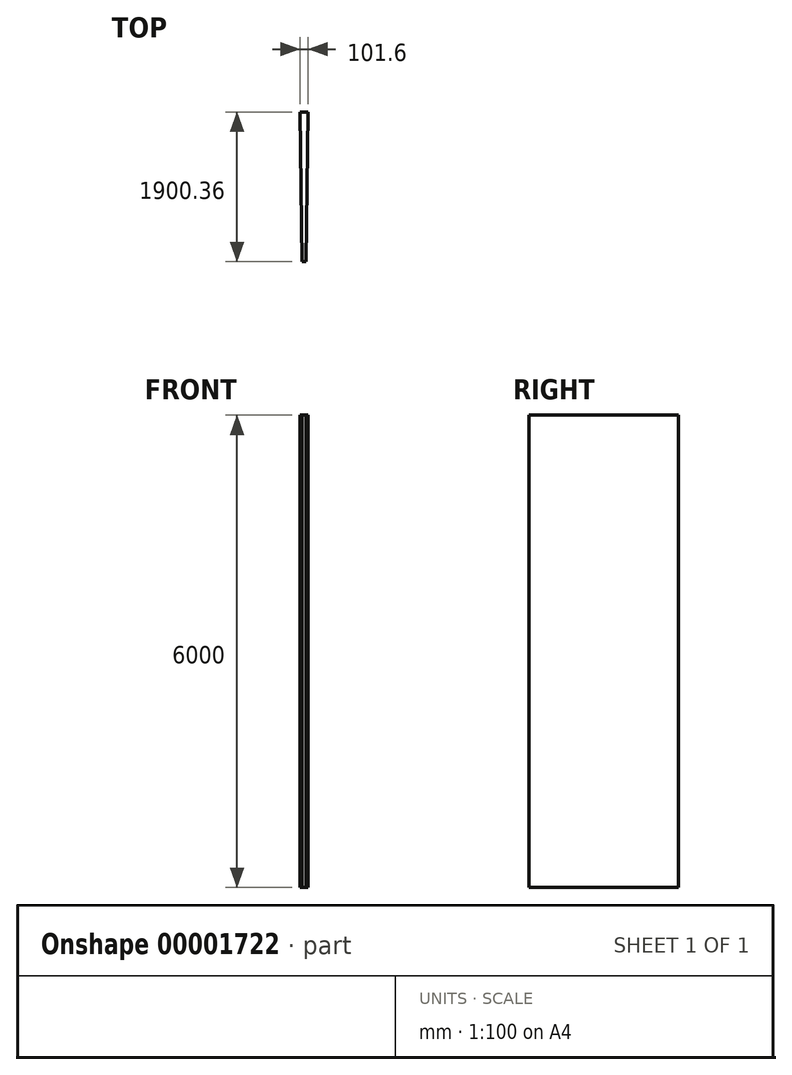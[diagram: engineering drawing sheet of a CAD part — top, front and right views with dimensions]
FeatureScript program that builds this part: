
annotation { "Feature Type Name" : "Feature", "Feature Type Description" : "" }
export const myFeature = defineFeature(function(context is Context, id is Id, definition is map)
    precondition{}
    {
        {
            var Q0;
            Q0=qCreatedBy(makeId("Top.planeOp"),FACE);
            var sketch = newSketch(context, id + "F0", { "sketchPlane" : qUnion([Q0])});
            skCircle(sketch, "E0", {"center": v(0, 0) * mm, "radius": 900 * mm, "construction": true});
            skLineSegment(sketch, "E1", {"start": v(0, 899.64) * mm, "end": v(0, 0) * mm, "construction": true});
            skLineSegment(sketch, "E2", {"start": v(-25.4, 899.64) * mm, "end": v(25.4, 899.64) * mm});
            skLineSegment(sketch, "E3", {"start": v(-25.4, 899.64) * mm, "end": v(-50.8, 2800) * mm});
            skLineSegment(sketch, "E4", {"start": v(-50.8, 2800) * mm, "end": v(50.8, 2800) * mm});
            skLineSegment(sketch, "E5", {"start": v(50.8, 2800) * mm, "end": v(25.4, 899.64) * mm});
            skLineSegment(sketch, "E6", {"start": v(0, 0) * mm, "end": v(0, 2800) * mm, "construction": true});
            skSolve(sketch);
        }
        {
            var Q0;
            Q0 = qSketchRegion(id + "F0", true);
            extrude(context, id + "F1", {"entities" : qUnion([Q0]), "depth" : 6000 * mm});
        }
    });
